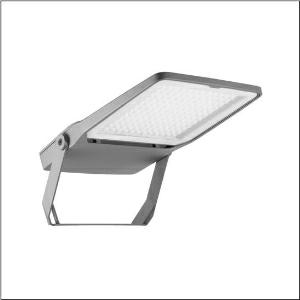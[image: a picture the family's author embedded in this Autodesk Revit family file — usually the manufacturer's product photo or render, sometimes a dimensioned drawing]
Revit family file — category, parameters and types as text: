
# Revit family: floodlight_fl_20_midi___pl43_5xa7682e1a1ac_2750
name_source: partatom
category: Lighting Fixtures
units: mm (PartAtom-declared; Revit-internal decimal feet)

## family parameters
Cut with Voids When Loaded = No
Host = Face
Light Source = No
Part Type = Normal
Room Calculation Point = No
Round Connector Dimension = Use Diameter
Shared = No

## types (1)
- --- (1 x LED 3000K / CRI = 80 (unbekannt), 22300 lm, 3000K)
    Apparent Load = 208 VA
    CIE Flux Codes = 32 74 99 100 100
    Color Rendering = 80
    Color Temperature = 3000K
    Default Elevation = 1800 mm
    Description = Floodlight FL 20 midi, floodlight, primary light control with lens, of plastic, primary optical cover: protective disc, of toughened safety glass, transparent, light distribution: PL43, light emission: direct distribution, primary light characteristic: asymmetric, installation type: surface-mounted, LED, High Power LED, rated luminous flux: 22.300lm, luminous efficacy: 107lm/W, light colour: 830, colour temperature: 3000K, control gear: ECG Plus, control: flexible luminous flux parameterisation, time-dependent luminous flux control, digital communication interface, power reduction, overheat protection, electronic power reduction, with terminal, 5-pole, max. 2.5mm², mains connection: 220..240V, AC, 50/60Hz, rated input power: 208W, LED unit, of diecast aluminium, powder-coated, Siteco® metallic grey (DB 702S), corrosivity category C5 mid according to DIN EN ISO 12944, incl. 1x M20 cable gland for cable Ø 6.5..12mm, length: 654mm, width: 450mm, height: 76mm, housing frame, of diecast aluminium, powder-coated, Siteco® metallic grey (DB 702S), mounting bracket, of steel, powder-coated, Siteco® metallic grey (DB 702S), DALI, protection rating (complete): IP66, insulation class (complete): insulation class II (safety insulation), certification: CE, ENEC, VDE, protection symbol: D, permissible operating ambient temperature: -40..+40°C, permissible operating ambient temperature for outdoor applications: -40..+50°C, standard: DIN EN 12944, packaging unit: 1 piece

Light Distribution: PL43
    Height = 76 mm
    Lamp = 1 x LED 3000K / CRI >= 80 (unbekannt)
    Lamp Light Flux = 22300 lm
    Lamp count = 1
    Length = 672 mm
    Luminous efficacy = 107 lm/W
    Manufacturer = Siteco
    ModVariant = No
    Model = 5XA7682E1A1AC
    Mounting Place = Wall
    Mounting Type = Surface mounted
    Number of Poles = 1
    OnlyDefault = Yes
    Power Factor = 1
    Product Name = Floodlight FL 20 midi | PL43
    Product group = floodlight | wall mounted
    ProductGroupID = 2001
    Protection Class = Protection class II
    Protection Degree = IP 66
    RLX_Detail_Level = 1
    RLX_Emergency_Light_Flux = 0 lm
    RLX_Emergency_Type = 0
    RLX_Emergency_Type_DB = No
    RlxData = <blob elided: 97893 chars, md5=80024b25>
    Socket = socket
    Standby Power = 0 W
    System Light Flux = 22300 lm
    System Power = 208 W
    Type Comments = factory setting: luminous flux: 100 % | dim-lin: 254 | 484 mA
    Type Image = l_1005943.jpg
    URL = http://relux.com
    VarID = @adj_148439
    Voltage = 0 V
    Weight = 0.00 kg
    Width = 450 mm

## geometry (parser evidence)
native form markers: Blend x4, Sweep x11
no freeform markers — native parametric forms only
